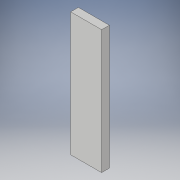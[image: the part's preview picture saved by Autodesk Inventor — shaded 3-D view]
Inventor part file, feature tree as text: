
AUTODESK INVENTOR PART (.ipt)
format: ipt  version: 2017 (Build 210142000, 142)  size: 90,112 bytes
history: native  units: in
note: dims shown in document units (in); Inventor stores cm internally (conversion verified against a paired STEP export)
features: extrude x1, sketch x1
ambient origin geometry x8: Origin, YZ Plane, XZ Plane, XY Plane, X Axis, Y Axis, Z Axis, Center Point
bodies: Solid1 (feature_tree)
feature tree (2):
  extrude  "Extrusion1"  Depth=2.0in
  sketch  "Sketch1"  dims[d0=8.0in d1=2.0in d2=0.5in d3=0.0in]
